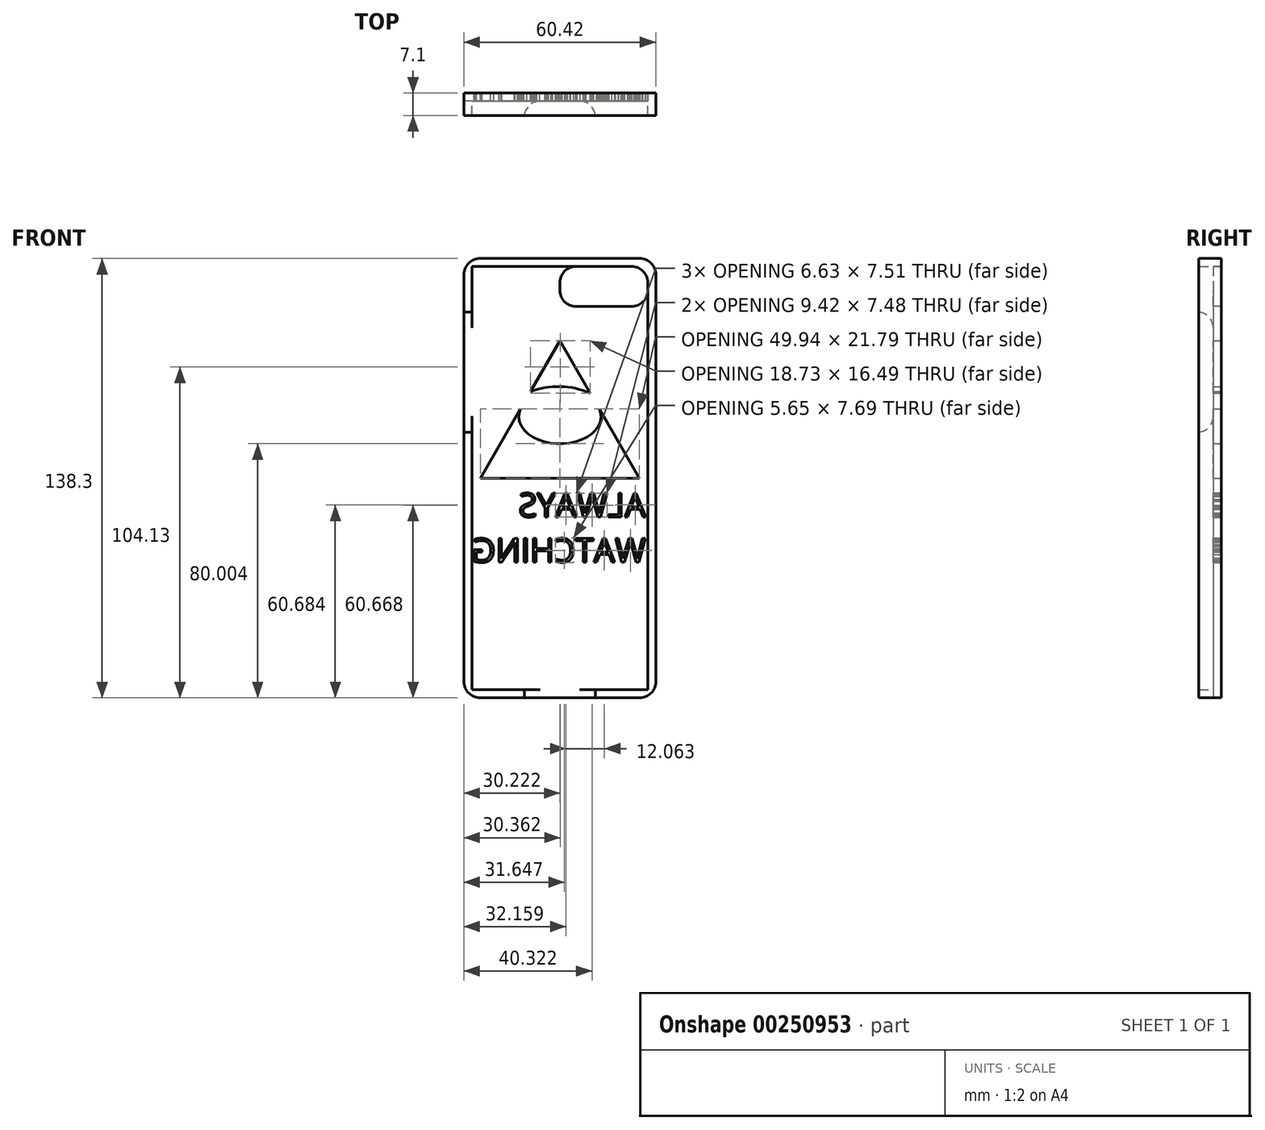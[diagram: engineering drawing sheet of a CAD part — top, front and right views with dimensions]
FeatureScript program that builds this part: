
annotation { "Feature Type Name" : "Feature", "Feature Type Description" : "" }
export const myFeature = defineFeature(function(context is Context, id is Id, definition is map)
    precondition{}
    {
        {
            var Q0;
            Q0=qCreatedBy(makeId("Front.planeOp"),FACE);
            var sketch = newSketch(context, id + "F0", { "sketchPlane" : qUnion([Q0])});
            skLineSegment(sketch, "E0.bottom", {"start": v(-30.2, 69.15) * mm, "end": v(30.2, 69.15) * mm});
            skLineSegment(sketch, "E0.top", {"start": v(-30.2, -69.15) * mm, "end": v(30.2, -69.15) * mm});
            skLineSegment(sketch, "E0.left", {"start": v(-30.2, 69.15) * mm, "end": v(-30.2, -69.15) * mm});
            skLineSegment(sketch, "E0.right", {"start": v(30.2, 69.15) * mm, "end": v(30.2, -69.15) * mm});
            skPoint(sketch, "E0.middle", {"position": v(0, 0) * mm});
            skSolve(sketch);
        }
        {
            var Q0;
            Q0=makeQuery(id+"F0.imprint","IMPRINT",FACE,{"disambiguationData":[TD([[makeQuery(id+"F0.imprint","IMPRINT",EDGE,{"derivedFrom":sQuery(id+"F0.wireOp",EDGE,"E0.bottom")}),-1.0]])]});
            extrude(context, id + "F1", {"entities" : qUnion([Q0]), "endBound" : BoundingType.SYMMETRIC, "depth" : 7.1 * mm});
        }
        {
            var Q0;
            Q0=makeQuery(id+"F1.opExtrude","CAP_FACE",FACE,{"disambiguationData":[OSD([sQuery(id+"F0.wireOp",EDGE,"E0.bottom"),sQuery(id+"F0.wireOp",EDGE,"E0.top"),sQuery(id+"F0.wireOp",EDGE,"E0.left"),sQuery(id+"F0.wireOp",EDGE,"E0.right")])],"isStart":false});
            shell(context, id + "F2", {"entities" : qUnion([Q0]), "thickness" : 2.54 * mm});
        }
        {
            var Q0;
            Q0=makeQuery(id+"F1.opExtrude","SWEPT_EDGE",EDGE,{"disambiguationData":[OSD([sQuery(id+"F0.wireOp",EDGE,"E0.bottom"),sQuery(id+"F0.wireOp",EDGE,"E0.left")])]});
            var Q1;
            Q1=makeQuery(id+"F1.opExtrude","SWEPT_EDGE",EDGE,{"disambiguationData":[OSD([sQuery(id+"F0.wireOp",EDGE,"E0.bottom"),sQuery(id+"F0.wireOp",EDGE,"E0.right")])]});
            var Q2;
            Q2=makeQuery(id+"F1.opExtrude","SWEPT_EDGE",EDGE,{"disambiguationData":[OSD([sQuery(id+"F0.wireOp",EDGE,"E0.top"),sQuery(id+"F0.wireOp",EDGE,"E0.left")])]});
            var Q3;
            Q3=makeQuery(id+"F1.opExtrude","SWEPT_EDGE",EDGE,{"disambiguationData":[OSD([sQuery(id+"F0.wireOp",EDGE,"E0.top"),sQuery(id+"F0.wireOp",EDGE,"E0.right")])]});
            fillet(context, id + "F3", {"entities" : qUnion([Q0, Q1, Q2, Q3]), "radius" : 5.08 * mm, "tangentPropagation" : true, "allowEdgeOverflow" : false});
        }
        {
            var Q0;
            Q0=makeQuery(id+"F2.opShell","OFFSET_FACE",FACE,{"disambiguationData":[OSD([sQuery(id+"F0.wireOp",EDGE,"E0.top")])]});
            var sketch = newSketch(context, id + "F4", { "sketchPlane" : qUnion([Q0])});
            skLineSegment(sketch, "E1.bottom", {"start": v(-11.19, 1) * mm, "end": v(11.18, 1) * mm});
            skLineSegment(sketch, "E1.top", {"start": v(-11.19, -3.55) * mm, "end": v(11.18, -3.55) * mm});
            skLineSegment(sketch, "E1.left", {"start": v(-11.19, 1) * mm, "end": v(-11.19, -3.55) * mm});
            skLineSegment(sketch, "E1.right", {"start": v(11.18, 1) * mm, "end": v(11.18, -3.55) * mm});
            skSolve(sketch);
        }
        {
            var Q0;
            Q0=makeQuery(id+"F4.imprint","IMPRINT",FACE,{"disambiguationData":[TD([[makeQuery(id+"F4.imprint","IMPRINT",EDGE,{"derivedFrom":sQuery(id+"F4.wireOp",EDGE,"E1.bottom")}),-1.0]])]});
            extrude(context, id + "F5", {"entities" : qUnion([Q0]), "operationType" : NewBodyOperationType.REMOVE, "oppositeDirection" : true, "depth" : 25 * mm});
        }
        {
            var Q0;
            Q0=makeQuery(id+"F5.boolean.opBoolean","MERGE",FACE,{"derivedFrom":[makeQuery(id+"F2.opShell","OFFSET_FACE",FACE,{"disambiguationData":[OSD([sQuery(id+"F0.wireOp",EDGE,"E0.bottom"),sQuery(id+"F0.wireOp",EDGE,"E0.top"),sQuery(id+"F0.wireOp",EDGE,"E0.left"),sQuery(id+"F0.wireOp",EDGE,"E0.right")])]}),makeQuery(id+"F5.opExtrude","SWEPT_FACE",FACE,{"disambiguationData":[OSD([sQuery(id+"F4.wireOp",EDGE,"E1.bottom")])]})]});
            var sketch = newSketch(context, id + "F6", { "sketchPlane" : qUnion([Q0])});
            skLineSegment(sketch, "E2.bottom", {"start": v(27.67, 66.61) * mm, "end": v(0, 66.61) * mm});
            skLineSegment(sketch, "E2.top", {"start": v(27.67, 54.08) * mm, "end": v(0, 54.08) * mm});
            skLineSegment(sketch, "E2.left", {"start": v(27.67, 66.61) * mm, "end": v(27.67, 54.08) * mm});
            skLineSegment(sketch, "E2.right", {"start": v(0, 66.61) * mm, "end": v(0, 54.08) * mm});
            skSolve(sketch);
        }
        {
            var Q0;
            Q0=makeQuery(id+"F6.imprint","IMPRINT",FACE,{"disambiguationData":[TD([[makeQuery(id+"F6.imprint","IMPRINT",EDGE,{"derivedFrom":sQuery(id+"F6.wireOp",EDGE,"E2.bottom")}),-1.0]])]});
            extrude(context, id + "F7", {"entities" : qUnion([Q0]), "operationType" : NewBodyOperationType.REMOVE, "oppositeDirection" : true, "depth" : 25 * mm});
        }
        {
            var Q0;
            Q0=makeQuery(id+"F7.boolean.opBoolean","COPY",EDGE,{"derivedFrom":makeQuery(id+"F7.opExtrude","SWEPT_EDGE",EDGE,{"disambiguationData":[OSD([sQuery(id+"F6.wireOp",EDGE,"E2.top"),sQuery(id+"F6.wireOp",EDGE,"E2.right")])]})});
            var Q1;
            Q1=makeQuery(id+"F7.boolean.opBoolean","COPY",EDGE,{"derivedFrom":makeQuery(id+"F7.opExtrude","SWEPT_EDGE",EDGE,{"disambiguationData":[OSD([sQuery(id+"F0.wireOp",EDGE,"E0.bottom"),sQuery(id+"F6.wireOp",EDGE,"E2.bottom"),sQuery(id+"F6.wireOp",EDGE,"E2.right")])]})});
            var Q2;
            Q2=makeQuery(id+"F7.boolean.opBoolean","COPY",EDGE,{"derivedFrom":makeQuery(id+"F7.opExtrude","SWEPT_EDGE",EDGE,{"disambiguationData":[OSD([sQuery(id+"F0.wireOp",EDGE,"E0.right"),sQuery(id+"F6.wireOp",EDGE,"E2.top"),sQuery(id+"F6.wireOp",EDGE,"E2.left")])]})});
            var Q3;
            Q3=makeQuery(id+"F7.boolean.opBoolean","MERGE",EDGE,{"derivedFrom":[makeQuery(id+"F2.opShell","OFFSET_EDGE",EDGE,{"disambiguationData":[OSD([sQuery(id+"F0.wireOp",EDGE,"E0.bottom"),sQuery(id+"F0.wireOp",EDGE,"E0.right")])]}),makeQuery(id+"F7.opExtrude","SWEPT_EDGE",EDGE,{"disambiguationData":[OSD([sQuery(id+"F6.wireOp",EDGE,"E2.bottom"),sQuery(id+"F6.wireOp",EDGE,"E2.left")])]})]});
            fillet(context, id + "F8", {"entities" : qUnion([Q0, Q1, Q2, Q3]), "radius" : 5 * mm, "tangentPropagation" : true, "allowEdgeOverflow" : false});
        }
        {
            var Q0;
            Q0=makeQuery(id+"F1.opExtrude","CAP_FACE",FACE,{"disambiguationData":[OSD([sQuery(id+"F0.wireOp",EDGE,"E0.bottom"),sQuery(id+"F0.wireOp",EDGE,"E0.top"),sQuery(id+"F0.wireOp",EDGE,"E0.left"),sQuery(id+"F0.wireOp",EDGE,"E0.right")])],"isStart":true});
            var sketch = newSketch(context, id + "F9", { "sketchPlane" : qUnion([Q0])});
            skSolve(sketch);
        }
        {
            var Q0;
            Q0=makeQuery(id+"F2.opShell","OFFSET_FACE",FACE,{"disambiguationData":[OSD([sQuery(id+"F0.wireOp",EDGE,"E0.left")])]});
            var sketch = newSketch(context, id + "F10", { "sketchPlane" : qUnion([Q0])});
            skLineSegment(sketch, "E3.bottom", {"start": v(1, 52.28) * mm, "end": v(-3.55, 52.28) * mm});
            skLineSegment(sketch, "E3.top", {"start": v(1, 14.48) * mm, "end": v(-3.55, 14.48) * mm});
            skLineSegment(sketch, "E3.left", {"start": v(1, 52.28) * mm, "end": v(1, 14.48) * mm});
            skLineSegment(sketch, "E3.right", {"start": v(-3.55, 52.28) * mm, "end": v(-3.55, 14.48) * mm});
            skSolve(sketch);
        }
        {
            var Q0;
            Q0=makeQuery(id+"F10.imprint","IMPRINT",FACE,{"disambiguationData":[TD([[makeQuery(id+"F10.imprint","IMPRINT",EDGE,{"derivedFrom":sQuery(id+"F10.wireOp",EDGE,"E3.bottom")}),1.0]])]});
            extrude(context, id + "F11", {"entities" : qUnion([Q0]), "operationType" : NewBodyOperationType.REMOVE, "oppositeDirection" : true, "depth" : 25 * mm});
        }
        {
            var Q0;
            Q0=makeQuery(id+"F11.boolean.opBoolean","COPY",EDGE,{"derivedFrom":makeQuery(id+"F11.opExtrude","SWEPT_EDGE",EDGE,{"disambiguationData":[OSD([sQuery(id+"F0.wireOp",EDGE,"E0.left"),sQuery(id+"F10.wireOp",EDGE,"E3.bottom"),sQuery(id+"F10.wireOp",EDGE,"E3.left")])]})});
            var Q1;
            Q1=makeQuery(id+"F11.boolean.opBoolean","COPY",EDGE,{"derivedFrom":makeQuery(id+"F11.opExtrude","SWEPT_EDGE",EDGE,{"disambiguationData":[OSD([sQuery(id+"F0.wireOp",EDGE,"E0.left"),sQuery(id+"F10.wireOp",EDGE,"E3.top"),sQuery(id+"F10.wireOp",EDGE,"E3.left")])]})});
            var Q2;
            Q2=makeQuery(id+"F5.boolean.opBoolean","COPY",EDGE,{"derivedFrom":makeQuery(id+"F5.opExtrude","SWEPT_EDGE",EDGE,{"disambiguationData":[OSD([sQuery(id+"F0.wireOp",EDGE,"E0.top"),sQuery(id+"F4.wireOp",EDGE,"E1.bottom"),sQuery(id+"F4.wireOp",EDGE,"E1.left")])]})});
            var Q3;
            Q3=makeQuery(id+"F5.boolean.opBoolean","COPY",EDGE,{"derivedFrom":makeQuery(id+"F5.opExtrude","SWEPT_EDGE",EDGE,{"disambiguationData":[OSD([sQuery(id+"F0.wireOp",EDGE,"E0.top"),sQuery(id+"F4.wireOp",EDGE,"E1.bottom"),sQuery(id+"F4.wireOp",EDGE,"E1.right")])]})});
            fillet(context, id + "F12", {"entities" : qUnion([Q0, Q1, Q2, Q3]), "radius" : 5 * mm, "tangentPropagation" : true, "allowEdgeOverflow" : false});
        }
        {
            var Q0;
            {var subQ3=sQuery(id+"F0.wireOp",EDGE,"E0.bottom");Q0=makeQuery(id+"F9.imprint","IMPRINT",FACE,{"disambiguationData":[TD([[makeQuery(id+"F9.imprint","IMPRINT",EDGE,{"derivedFrom":makeQuery(id+"F1.opExtrude","CAP_EDGE",EDGE,{"disambiguationData":[OSD([subQ3])],"isStart":true})}),1.0]])]});}
            var sketch = newSketch(context, id + "F13", { "sketchPlane" : qUnion([Q0])});
            skLineSegment(sketch, "E4.0", {"start": v(-24.98, 0) * mm, "end": v(0.02, 43.23) * mm});
            skLineSegment(sketch, "E4.1", {"start": v(0.02, 43.23) * mm, "end": v(24.96, -0.04) * mm});
            skLineSegment(sketch, "E4.2", {"start": v(24.96, -0.04) * mm, "end": v(-24.98, 0) * mm});
            skPoint(sketch, "E4.0.midPoint", {"position": v(-12.48, 21.61) * mm});
            skEllipticalArc(sketch, "E5", {});
            skArc(sketch, "E6", {"start": v(-12.05, 29.4) * mm, "mid": v(0.15, 16.77) * mm, "end": v(12.05, 29.7) * mm});
            skArc(sketch, "E7", {"start": v(18.07, 21.61) * mm, "mid": v(1.18, 28.84) * mm, "end": v(-16.07, 22.52) * mm});
            const initialGuessF13  = {"E5": [0, 0.01936475560069084, -1, 0, 0.012909836135804653, 0.008568861667849226, 5.593703002525991, 3.8310749582607473]};
            skSetInitialGuess(sketch, initialGuessF13);
            skSolve(sketch);
        }
        {
            var Q0;
            {var subQ0=sQuery(id+"F13.wireOp",EDGE,"E4.2");Q0=makeQuery(id+"F13.imprint","IMPRINT",FACE,{"disambiguationData":[TD([[makeQuery(id+"F13.imprint","IMPRINT",EDGE,{"derivedFrom":subQ0}),-1.0]])]});}
            var Q1;
            {var subQ0=sQuery(id+"F13.wireOp",EDGE,"E4.1");var subQ1=sQuery(id+"F13.wireOp",EDGE,"E4.0");var subQ2=makeQuery(id+"F13.imprint","INTERSECT",VERTEX,{"derivedFrom":[subQ1,subQ0]});Q1=makeQuery(id+"F13.imprint","IMPRINT",FACE,{"disambiguationData":[TD([[makeQuery(id+"F13.imprint","IMPRINT",EDGE,{"disambiguationData":[TD([[subQ2,1.0]])],"derivedFrom":subQ1}),-1.0]])]});}
            extrude(context, id + "F14", {"entities" : qUnion([Q0, Q1]), "operationType" : NewBodyOperationType.REMOVE, "endBound" : BoundingType.SYMMETRIC, "oppositeDirection" : true, "depth" : 25 * mm});
        }
        {
            var Q0;
            {var subQ3=sQuery(id+"F0.wireOp",EDGE,"E0.bottom");Q0=makeQuery(id+"F9.imprint","IMPRINT",FACE,{"disambiguationData":[TD([[makeQuery(id+"F9.imprint","IMPRINT",EDGE,{"derivedFrom":makeQuery(id+"F1.opExtrude","CAP_EDGE",EDGE,{"disambiguationData":[OSD([subQ3])],"isStart":true})}),1.0]])]});}
            var sketch = newSketch(context, id + "F15", { "sketchPlane" : qUnion([Q0])});
            skText(sketch, "E8", { "text": "ALWAYS\nWATCHING", "fontName": "OpenSans-Regular.ttf"});
            const initialGuessF15  = {"E8": [-0.02702, -0.01222, 1, 0, 0.00754]};
            skSetInitialGuess(sketch, initialGuessF15);
            skSolve(sketch);
        }
        {
            var Q0;
            Q0 = qSketchRegion(id + "F15", true);
            extrude(context, id + "F16", {"entities" : qUnion([Q0]), "operationType" : NewBodyOperationType.REMOVE, "oppositeDirection" : true, "depth" : 25 * mm});
        }
    });
